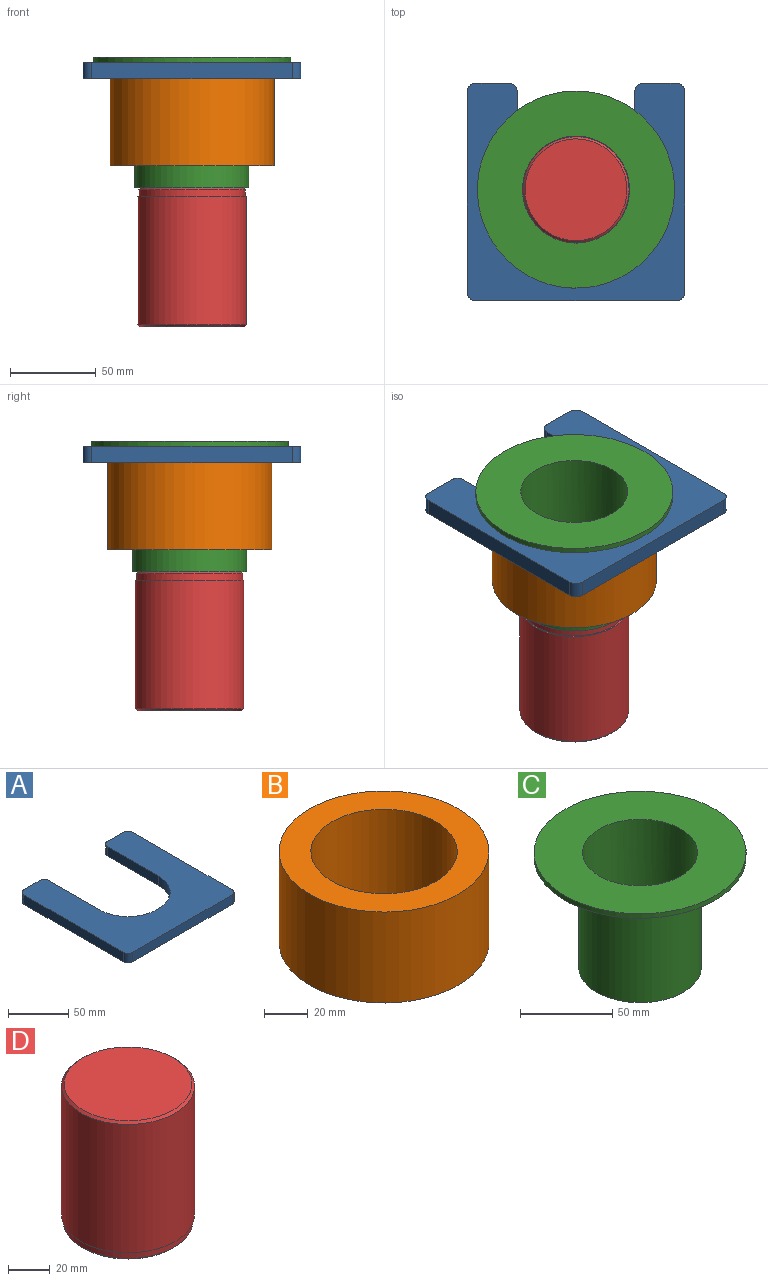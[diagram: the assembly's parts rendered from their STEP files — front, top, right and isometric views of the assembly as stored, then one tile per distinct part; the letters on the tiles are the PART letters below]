
ASSEMBLY  parts=4 mates=3
PART A: 18 faces, bbox 127x127x9.5 mm
  f0: plane 19.05x9.53mm, normal (0,1,0), area 181.5mm2, adj f5,f6,f13,f16
  f1: plane 116.84x9.53mm, normal (-1,0,0), area 1112.9mm2, adj f5,f6,f14,f17
  f2: plane 116.84x9.53mm, normal (0,-1,0), area 1112.9mm2, adj f5,f6,f14,f15
  f3: plane 116.84x9.53mm, normal (1,0,0), area 1112.9mm2, adj f5,f6,f15,f16
  f4: plane 19.05x9.53mm, normal (0,1,0), area 181.5mm2, adj f5,f6,f12,f17
  f5: plane 127x127mm, normal (0,0,1), area 9857.3mm2, adj f0,f1,f2,f3,f4,f7,f8,f9
  f6: plane 127x127mm, normal (0,0,-1), area 9857.3mm2, adj f0,f1,f2,f3,f4,f7,f8,f9
  f7: plane 59.69x9.53mm, normal (1,0,0), area 568.5mm2, adj f5,f6,f10,f12
  f8: plane 9.53x2.54mm, normal (0,1,0), area 24.2mm2, adj f5,f6,f10,f11
  f9: plane 59.69x9.53mm, normal (-1,0,0), area 568.5mm2, adj f5,f6,f11,f13
  f10: cylinder r=33.02mm len=33.02mm, axis (0,0,-1), area 494mm2, adj f5,f6,f7,f8
  f11: cylinder r=33.02mm len=33.02mm, axis (0,0,1), area 494mm2, adj f5,f6,f8,f9
  f12: cylinder r=5.08mm len=9.53mm, axis (0,0,-1), area 76mm2, adj f4,f5,f6,f7
  f13: cylinder r=5.08mm len=9.53mm, axis (0,0,1), area 76mm2, adj f0,f5,f6,f9
  f14: cylinder r=5.08mm len=9.53mm, axis (0,0,1), area 76mm2, adj f1,f2,f5,f6
  f15: cylinder r=5.08mm len=9.53mm, axis (0,0,-1), area 76mm2, adj f2,f3,f5,f6
  f16: cylinder r=5.08mm len=9.53mm, axis (0,0,1), area 76mm2, adj f0,f3,f5,f6
  f17: cylinder r=5.08mm len=9.53mm, axis (0,0,-1), area 76mm2, adj f1,f4,f5,f6
PART B: 4 faces, bbox 95.8x95.8x50.8 mm
  f0: cylinder r=47.88mm len=95.76mm, axis (0,0,-1), area 15282.3mm2, adj f1,f2
  f1: plane 95.76x95.76mm, normal (0,0,1), area 3696.9mm2, adj f0,f3
  f2: plane 95.76x95.76mm, normal (0,0,-1), area 3696.9mm2, adj f0,f3
  f3: cylinder r=33.4mm len=66.8mm, axis (0,0,1), area 10661.1mm2, adj f1,f2
PART C: 6 faces, bbox 115.1x115.1x76.2 mm
  f0: cylinder r=57.53mm len=115.06mm, axis (0,0,-1), area 1101.8mm2, adj f1,f3
  f1: plane 115.06x115.06mm, normal (0,0,1), area 7331.7mm2, adj f0,f5
  f2: cylinder r=33.27mm len=73.15mm, axis (0,0,-1), area 15293.6mm2, adj f3,f4
  f3: plane 115.06x115.06mm, normal (0,0,-1), area 6919.9mm2, adj f0,f2
  f4: plane 66.55x66.55mm, normal (0,0,-1), area 411.9mm2, adj f2,f5
  f5: cylinder r=31.24mm len=76.2mm, axis (0,0,-1), area 14958mm2, adj f1,f4
PART D: 7 faces, bbox 63.5x63.5x81.3 mm
  f0: cylinder r=30.99mm len=61.98mm, axis (0,0,-1), area 741.8mm2, adj f4,f5
  f1: plane 59.44x59.44mm, normal (0,0,-1), area 2774.5mm2, adj f5
  f2: cylinder r=31.75mm len=74.93mm, axis (0,0,-1), area 14947.9mm2, adj f4,f6
  f3: plane 60.96x60.96mm, normal (0,0,1), area 2918.6mm2, adj f6
  f4: plane 63.5x63.5mm, normal (0,0,-1), area 150.2mm2, adj f0,f2
  f5: cone r=30.99mm half-angle=45deg, axis (0,0,1), area 342.5mm2, adj f0,f1
  f6: cone r=30.48mm half-angle=45deg, axis (0,0,-1), area 351.1mm2, adj f2,f3
PLACE A t=(-101.52,-50.67,107.08)mm
PLACE B t=(-38.02,14.25,56.15)mm
PLACE C t=(-38.02,14.25,43.45)mm
PLACE D rot(axis=(1,0,0),180deg) t=(-38.02,14.25,43.45)mm
MATE fastened D.f0 <-> C.f5  axis (0,0,1) through (-38.02,14.25,43.45)mm
MATE fastened B.f3 <-> C.f5  axis (0,0,1) through (-38.02,14.25,106.95)mm
MATE fastened A.f5 <-> C.f3  axis (0,0,1) through (-38.02,1.55,116.6)mm
